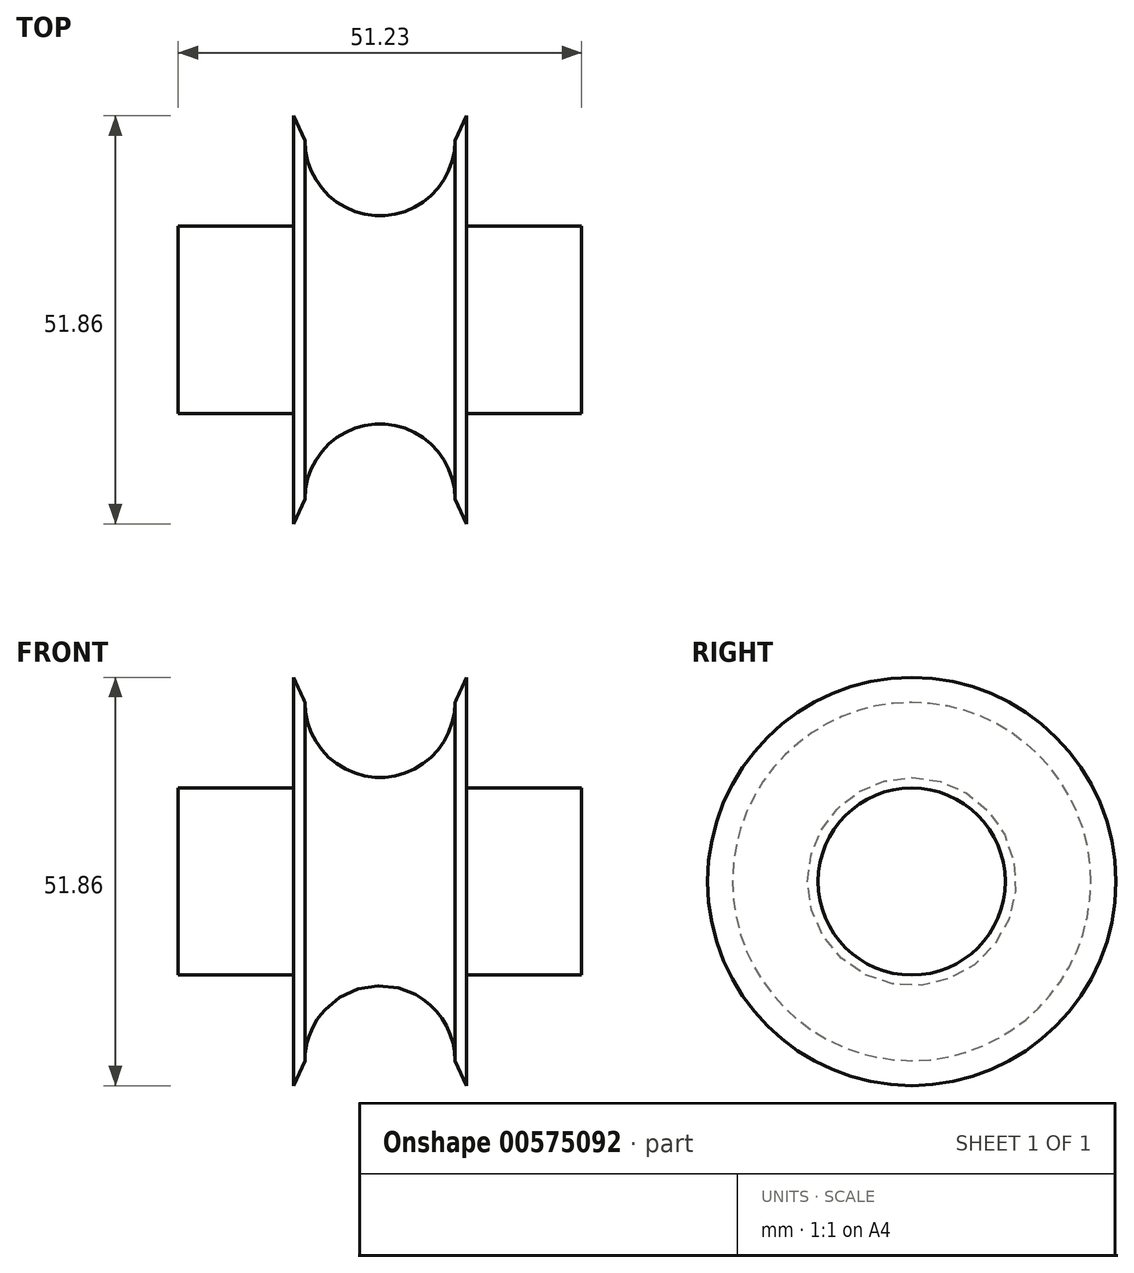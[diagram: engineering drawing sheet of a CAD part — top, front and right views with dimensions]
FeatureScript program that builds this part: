
annotation { "Feature Type Name" : "Feature", "Feature Type Description" : "" }
export const myFeature = defineFeature(function(context is Context, id is Id, definition is map)
    precondition{}
    {
        {
            var Q0;
            Q0=qCreatedBy(makeId("Front.planeOp"),FACE);
            var sketch = newSketch(context, id + "F0", { "sketchPlane" : qUnion([Q0])});
            skLineSegment(sketch, "E0", {"start": v(-20.97, 0) * mm, "end": v(30.26, 0) * mm});
            skLineSegment(sketch, "E1", {"start": v(-20.97, 11.89) * mm, "end": v(-20.97, 0) * mm});
            skArc(sketch, "E2", {"start": v(-4.88, 22.75) * mm, "mid": v(-2.1, 16.02) * mm, "end": v(4.64, 13.23) * mm});
            skLineSegment(sketch, "E3", {"start": v(4.64, 29.83) * mm, "end": v(4.64, -24.7) * mm, "construction": true});
            skLineSegment(sketch, "E4.MirrorCS", {"start": v(30.26, 11.89) * mm, "end": v(30.26, 0) * mm});
            skLineSegment(sketch, "E5", {"start": v(-4.88, 22.75) * mm, "end": v(-6.36, 25.93) * mm});
            skLineSegment(sketch, "E6", {"start": v(-6.36, 25.93) * mm, "end": v(-6.36, 0) * mm});
            skLineSegment(sketch, "E7", {"start": v(-20.97, 11.89) * mm, "end": v(-6.36, 11.89) * mm});
            skPoint(sketch, "E7.endSnap0", {"position": v(-6.36, 12.96) * mm});
            skArc(sketch, "E8.MirrorCS", {"start": v(14.17, 22.75) * mm, "mid": v(11.38, 16.02) * mm, "end": v(4.64, 13.23) * mm});
            skLineSegment(sketch, "E9.MirrorCS", {"start": v(14.17, 22.75) * mm, "end": v(15.65, 25.93) * mm});
            skLineSegment(sketch, "E10.MirrorCS", {"start": v(15.65, 25.93) * mm, "end": v(15.65, 0) * mm});
            skLineSegment(sketch, "E11.MirrorCS", {"start": v(30.26, 11.89) * mm, "end": v(15.65, 11.89) * mm});
            skSolve(sketch);
        }
        {
            var Q0;
            Q0 = qSketchRegion(id + "F0", true);
            var Q1;
            Q1=sQuery(id+"F0.wireOp",EDGE,"E0");
            revolve(context, id + "F1", {"entities" : qUnion([Q0]), "axis" : qUnion([Q1]), "revolveType" : RevolveType.FULL});
        }
    });
